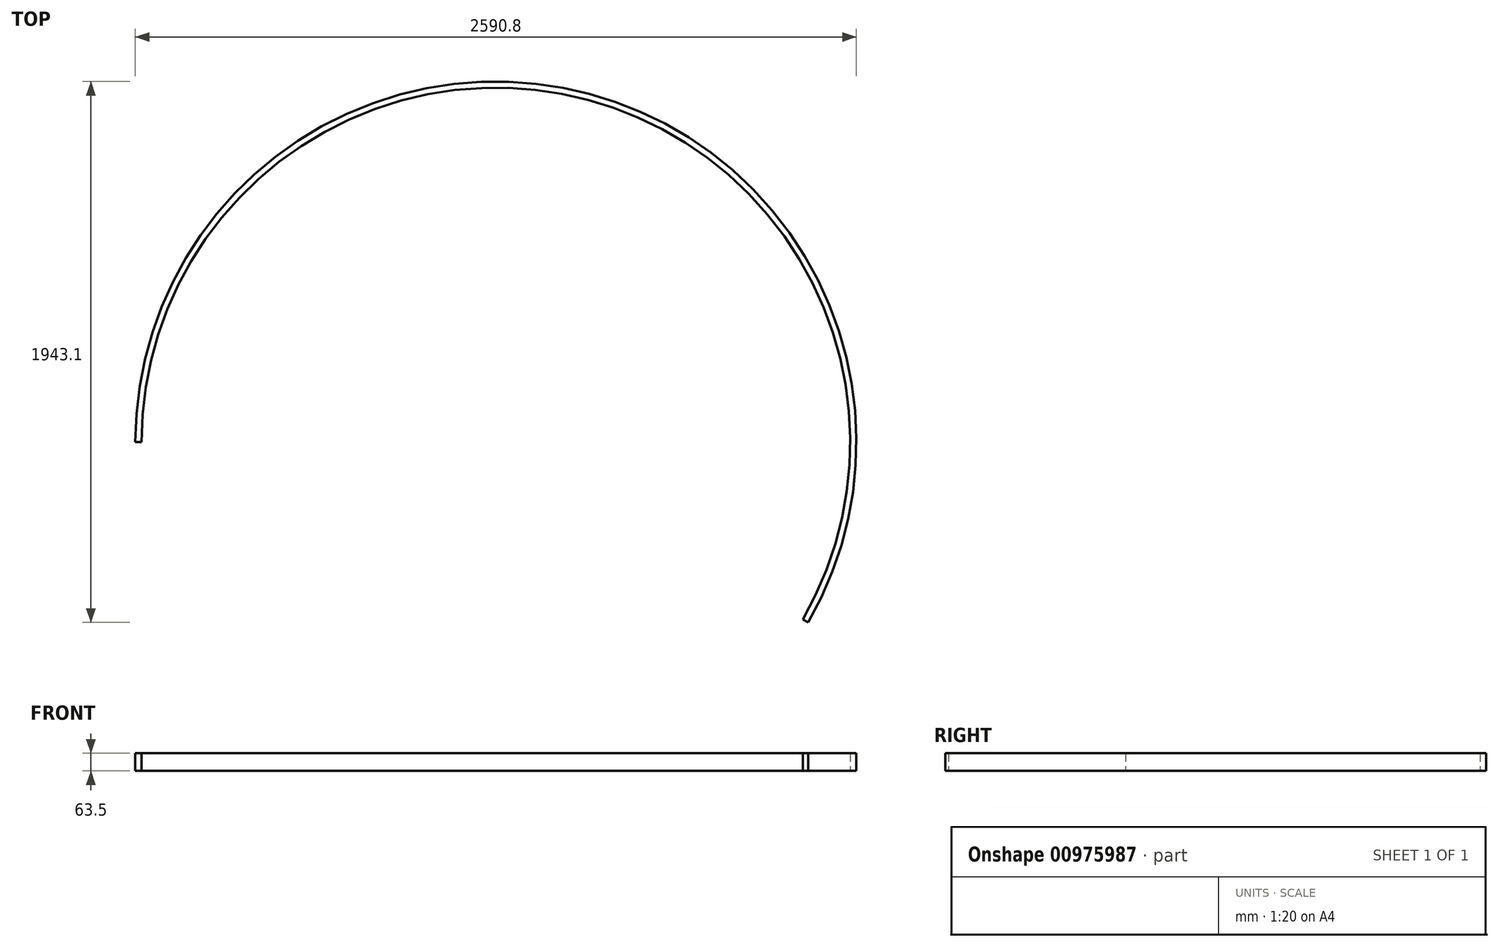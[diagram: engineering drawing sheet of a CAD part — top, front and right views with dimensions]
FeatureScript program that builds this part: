
annotation { "Feature Type Name" : "Feature", "Feature Type Description" : "" }
export const myFeature = defineFeature(function(context is Context, id is Id, definition is map)
    precondition{}
    {
        {
            var Q0;
            Q0=qCreatedBy(makeId("Top.planeOp"),FACE);
            var sketch = newSketch(context, id + "F0", { "sketchPlane" : qUnion([Q0])});
            skCircle(sketch, "E0", {"center": v(0, 0) * mm, "radius": 1295.4 * mm, "construction": true});
            skLineSegment(sketch, "E1", {"start": v(0, 0) * mm, "end": v(-1295.4, 0) * mm, "construction": true});
            skLineSegment(sketch, "E2", {"start": v(0, 0) * mm, "end": v(1121.85, -647.7) * mm, "construction": true});
            skArc(sketch, "E3", {"start": v(1121.85, -647.7) * mm, "mid": v(335.27, 1251.26) * mm, "end": v(-1295.4, 0) * mm});
            skArc(sketch, "E4.0", {"start": v(1102.6, -636.59) * mm, "mid": v(-1099.37, 642.15) * mm, "end": v(1096.11, -647.7) * mm, "construction": true});
            skArc(sketch, "E5", {"start": v(1102.6, -636.59) * mm, "mid": v(329.52, 1229.8) * mm, "end": v(-1273.18, 0) * mm});
            skLineSegment(sketch, "E6", {"start": v(-1273.18, 0) * mm, "end": v(-1295.4, 0) * mm});
            skLineSegment(sketch, "E7", {"start": v(1121.85, -647.7) * mm, "end": v(1102.6, -636.59) * mm});
            skSolve(sketch);
        }
        {
            var Q0;
            Q0 = qSketchRegion(id + "F0", true);
            extrude(context, id + "F1", {"entities" : qUnion([Q0]), "depth" : 63.5 * mm, "offsetDistance" : 25.4 * mm});
        }
    });
